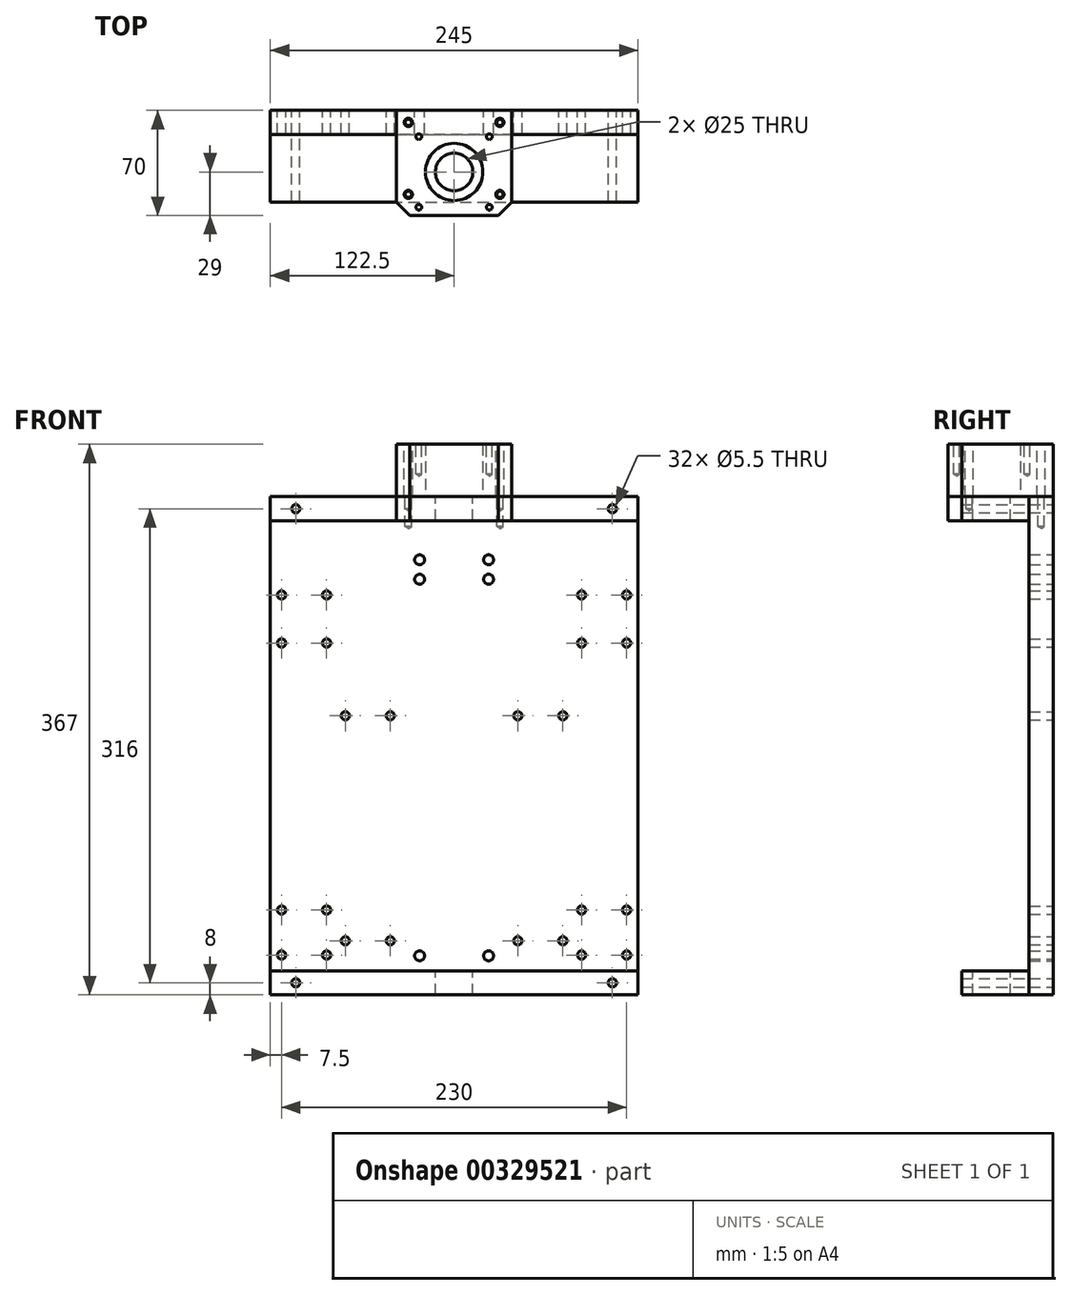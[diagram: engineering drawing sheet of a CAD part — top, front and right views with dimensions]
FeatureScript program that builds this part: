
annotation { "Feature Type Name" : "Feature", "Feature Type Description" : "" }
export const myFeature = defineFeature(function(context is Context, id is Id, definition is map)
    precondition{}
    {
        {
            var Q0;
            Q0=qCreatedBy(makeId("Front.planeOp"),FACE);
            var sketch = newSketch(context, id + "F0", { "sketchPlane" : qUnion([Q0])});
            skLineSegment(sketch, "E0.bottom", {"start": v(120.5, 166) * mm, "end": v(-120.5, 166) * mm});
            skLineSegment(sketch, "E0.top", {"start": v(120.5, -166) * mm, "end": v(-120.5, -166) * mm});
            skLineSegment(sketch, "E0.left", {"start": v(122.5, 164) * mm, "end": v(122.5, -164) * mm});
            skLineSegment(sketch, "E0.right", {"start": v(-122.5, 164) * mm, "end": v(-122.5, -164) * mm});
            skPoint(sketch, "E0.middle", {"position": v(0, 0) * mm});
            skPoint(sketch, "E1.visualSharp", {"position": v(-122.5, 166) * mm});
            skArc(sketch, "E1.filletArc", {"start": v(-120.5, 166) * mm, "mid": v(-121.91, 165.41) * mm, "end": v(-122.5, 164) * mm});
            skPoint(sketch, "E2.visualSharp", {"position": v(122.5, 166) * mm});
            skArc(sketch, "E2.filletArc", {"start": v(122.5, 164) * mm, "mid": v(121.91, 165.41) * mm, "end": v(120.5, 166) * mm});
            skPoint(sketch, "E3.visualSharp", {"position": v(122.5, -166) * mm});
            skArc(sketch, "E3.filletArc", {"start": v(120.5, -166) * mm, "mid": v(121.91, -165.41) * mm, "end": v(122.5, -164) * mm});
            skPoint(sketch, "E4.visualSharp", {"position": v(-122.5, -166) * mm});
            skArc(sketch, "E4.filletArc", {"start": v(-122.5, -164) * mm, "mid": v(-121.91, -165.41) * mm, "end": v(-120.5, -166) * mm});
            skCircle(sketch, "E5", {"center": v(-115, 100.5) * mm, "radius": 2.75 * mm});
            skCircle(sketch, "E6", {"center": v(-85, 100.5) * mm, "radius": 2.75 * mm});
            skCircle(sketch, "E7", {"center": v(-115, 68.5) * mm, "radius": 2.75 * mm});
            skCircle(sketch, "E8", {"center": v(-85, 68.5) * mm, "radius": 2.75 * mm});
            skCircle(sketch, "E9", {"center": v(-115, -109.5) * mm, "radius": 2.75 * mm});
            skCircle(sketch, "E10", {"center": v(-85, -109.5) * mm, "radius": 2.75 * mm});
            skCircle(sketch, "E11", {"center": v(-115, -139.5) * mm, "radius": 2.75 * mm});
            skCircle(sketch, "E12", {"center": v(-85, -139.5) * mm, "radius": 2.75 * mm});
            skCircle(sketch, "E13", {"center": v(85, -109.5) * mm, "radius": 2.75 * mm});
            skCircle(sketch, "E14", {"center": v(115, -109.5) * mm, "radius": 2.75 * mm});
            skCircle(sketch, "E15", {"center": v(85, -139.5) * mm, "radius": 2.75 * mm});
            skCircle(sketch, "E16", {"center": v(115, -139.5) * mm, "radius": 2.75 * mm});
            skCircle(sketch, "E17", {"center": v(85, 100.5) * mm, "radius": 2.75 * mm});
            skCircle(sketch, "E18", {"center": v(115, 100.5) * mm, "radius": 2.75 * mm});
            skCircle(sketch, "E19", {"center": v(85, 68.5) * mm, "radius": 2.75 * mm});
            skCircle(sketch, "E20", {"center": v(115, 68.5) * mm, "radius": 2.75 * mm});
            skCircle(sketch, "E21", {"center": v(-72.5, -130) * mm, "radius": 2.75 * mm});
            skCircle(sketch, "E22", {"center": v(-42.5, -130) * mm, "radius": 2.75 * mm});
            skCircle(sketch, "E23", {"center": v(-72.5, 20) * mm, "radius": 2.75 * mm});
            skCircle(sketch, "E24", {"center": v(-42.5, 20) * mm, "radius": 2.75 * mm});
            skCircle(sketch, "E25", {"center": v(42.5, 20) * mm, "radius": 2.75 * mm});
            skCircle(sketch, "E26", {"center": v(72.5, 20) * mm, "radius": 2.75 * mm});
            skCircle(sketch, "E27", {"center": v(42.5, -130) * mm, "radius": 2.75 * mm});
            skCircle(sketch, "E28", {"center": v(72.5, -130) * mm, "radius": 2.75 * mm});
            skCircle(sketch, "E29", {"center": v(-23, 124) * mm, "radius": 3.3 * mm});
            skCircle(sketch, "E30", {"center": v(23, 124) * mm, "radius": 3.3 * mm});
            skCircle(sketch, "E31", {"center": v(-23, -140) * mm, "radius": 3.3 * mm});
            skCircle(sketch, "E32", {"center": v(23, -140) * mm, "radius": 3.3 * mm});
            skCircle(sketch, "E33", {"center": v(-23, 111) * mm, "radius": 3.3 * mm});
            skCircle(sketch, "E34", {"center": v(23, 111) * mm, "radius": 3.3 * mm});
            skCircle(sketch, "E35", {"center": v(-105.5, 158) * mm, "radius": 2.75 * mm});
            skCircle(sketch, "E36", {"center": v(105.5, 158) * mm, "radius": 2.75 * mm});
            skCircle(sketch, "E37", {"center": v(-105.5, -158) * mm, "radius": 2.75 * mm});
            skCircle(sketch, "E38", {"center": v(105.5, -158) * mm, "radius": 2.75 * mm});
            skSolve(sketch);
        }
        {
            var Q0;
            Q0 = qSketchRegion(id + "F0", true);
            extrude(context, id + "F1", {"entities" : qUnion([Q0]), "depth" : 16 * mm});
        }
        {
            var Q0;
            Q0=makeQuery(id+"F1.opExtrude","CAP_FACE",FACE,{"disambiguationData":[OSD([sQuery(id+"F0.wireOp",EDGE,"E0.bottom"),sQuery(id+"F0.wireOp",EDGE,"E0.top"),sQuery(id+"F0.wireOp",EDGE,"E0.left"),sQuery(id+"F0.wireOp",EDGE,"E0.right"),sQuery(id+"F0.wireOp",EDGE,"E1.filletArc"),sQuery(id+"F0.wireOp",EDGE,"E2.filletArc"),sQuery(id+"F0.wireOp",EDGE,"E3.filletArc"),sQuery(id+"F0.wireOp",EDGE,"E4.filletArc"),sQuery(id+"F0.wireOp",EDGE,"E5"),sQuery(id+"F0.wireOp",EDGE,"E6"),sQuery(id+"F0.wireOp",EDGE,"E7"),sQuery(id+"F0.wireOp",EDGE,"E8"),sQuery(id+"F0.wireOp",EDGE,"E9"),sQuery(id+"F0.wireOp",EDGE,"E10"),sQuery(id+"F0.wireOp",EDGE,"E11"),sQuery(id+"F0.wireOp",EDGE,"E12"),sQuery(id+"F0.wireOp",EDGE,"E13"),sQuery(id+"F0.wireOp",EDGE,"E14"),sQuery(id+"F0.wireOp",EDGE,"E15"),sQuery(id+"F0.wireOp",EDGE,"E16"),sQuery(id+"F0.wireOp",EDGE,"E17"),sQuery(id+"F0.wireOp",EDGE,"E18"),sQuery(id+"F0.wireOp",EDGE,"E19"),sQuery(id+"F0.wireOp",EDGE,"E20"),sQuery(id+"F0.wireOp",EDGE,"E21"),sQuery(id+"F0.wireOp",EDGE,"E22"),sQuery(id+"F0.wireOp",EDGE,"E23"),sQuery(id+"F0.wireOp",EDGE,"E24"),sQuery(id+"F0.wireOp",EDGE,"E25"),sQuery(id+"F0.wireOp",EDGE,"E26"),sQuery(id+"F0.wireOp",EDGE,"E27"),sQuery(id+"F0.wireOp",EDGE,"E28"),sQuery(id+"F0.wireOp",EDGE,"E29"),sQuery(id+"F0.wireOp",EDGE,"E30"),sQuery(id+"F0.wireOp",EDGE,"E31"),sQuery(id+"F0.wireOp",EDGE,"E32"),sQuery(id+"F0.wireOp",EDGE,"E33"),sQuery(id+"F0.wireOp",EDGE,"E34"),sQuery(id+"F0.wireOp",EDGE,"E35"),sQuery(id+"F0.wireOp",EDGE,"E36"),sQuery(id+"F0.wireOp",EDGE,"E37"),sQuery(id+"F0.wireOp",EDGE,"E38")])],"isStart":false});
            var sketch = newSketch(context, id + "F2", { "sketchPlane" : qUnion([Q0])});
            skLineSegment(sketch, "E39.bottom", {"start": v(-122.5, 166) * mm, "end": v(122.5, 166) * mm});
            skLineSegment(sketch, "E39.top", {"start": v(-122.5, 150) * mm, "end": v(122.5, 150) * mm});
            skLineSegment(sketch, "E39.left", {"start": v(-122.5, 166) * mm, "end": v(-122.5, 150) * mm});
            skLineSegment(sketch, "E39.right", {"start": v(122.5, 166) * mm, "end": v(122.5, 150) * mm});
            skCircle(sketch, "E40", {"center": v(-105.5, 158) * mm, "radius": 2.75 * mm});
            skCircle(sketch, "E41", {"center": v(105.5, 158) * mm, "radius": 2.75 * mm});
            skLineSegment(sketch, "E42.bottom", {"start": v(-122.5, -150) * mm, "end": v(122.5, -150) * mm});
            skLineSegment(sketch, "E42.top", {"start": v(-122.5, -166) * mm, "end": v(122.5, -166) * mm});
            skLineSegment(sketch, "E42.left", {"start": v(-122.5, -150) * mm, "end": v(-122.5, -166) * mm});
            skLineSegment(sketch, "E42.right", {"start": v(122.5, -150) * mm, "end": v(122.5, -166) * mm});
            skCircle(sketch, "E43", {"center": v(-105.5, -158) * mm, "radius": 2.75 * mm});
            skCircle(sketch, "E44", {"center": v(105.5, -158) * mm, "radius": 2.75 * mm});
            skSolve(sketch);
        }
        {
            var Q0;
            Q0 = qSketchRegion(id + "F2", true);
            extrude(context, id + "F3", {"entities" : qUnion([Q0]), "depth" : 45 * mm});
        }
        {
            var Q0;
            Q0=makeQuery(id+"F3.opExtrude","SWEPT_FACE",FACE,{"disambiguationData":[OSD([sQuery(id+"F2.wireOp",EDGE,"E39.bottom")])]});
            var sketch = newSketch(context, id + "F4", { "sketchPlane" : qUnion([Q0])});
            skCircle(sketch, "E45", {"center": v(0, -41) * mm, "radius": 12.5 * mm});
            skSolve(sketch);
        }
        {
            var Q0;
            Q0 = qSketchRegion(id + "F4", true);
            extrude(context, id + "F5", {"entities" : qUnion([Q0]), "operationType" : NewBodyOperationType.REMOVE, "endBound" : BoundingType.THROUGH_ALL, "oppositeDirection" : true, "depth" : 25 * mm});
        }
        {
            var Q0;
            Q0=makeQuery(id+"F3.opExtrude","SWEPT_FACE",FACE,{"disambiguationData":[OSD([sQuery(id+"F2.wireOp",EDGE,"E39.bottom")])]});
            var sketch = newSketch(context, id + "F6", { "sketchPlane" : qUnion([Q0])});
            skLineSegment(sketch, "E46", {"start": v(-38.5, -61) * mm, "end": v(-29.5, -70) * mm});
            skLineSegment(sketch, "E47", {"start": v(-29.5, -70) * mm, "end": v(29.5, -70) * mm});
            skLineSegment(sketch, "E48", {"start": v(29.5, -70) * mm, "end": v(38.5, -61) * mm});
            skLineSegment(sketch, "E49", {"start": v(38.5, -61) * mm, "end": v(-38.5, -61) * mm});
            skPoint(sketch, "E50", {"position": v(0, -41) * mm});
            skSolve(sketch);
        }
        {
            var Q0;
            Q0 = qSketchRegion(id + "F6", true);
            extrude(context, id + "F7", {"entities" : qUnion([Q0]), "operationType" : NewBodyOperationType.ADD, "oppositeDirection" : true, "depth" : 16 * mm});
        }
        {
            var Q0;
            Q0=makeQuery(id+"F7.boolean.opBoolean","MERGE",FACE,{"derivedFrom":[makeQuery(id+"F3.opExtrude","SWEPT_FACE",FACE,{"disambiguationData":[OSD([sQuery(id+"F2.wireOp",EDGE,"E39.bottom")])]}),makeQuery(id+"F7.opExtrude","CAP_FACE",FACE,{"disambiguationData":[OSD([sQuery(id+"F6.wireOp",EDGE,"E46"),sQuery(id+"F6.wireOp",EDGE,"E47"),sQuery(id+"F6.wireOp",EDGE,"E48"),sQuery(id+"F6.wireOp",EDGE,"E49")])],"isStart":true})]});
            var sketch = newSketch(context, id + "F8", { "sketchPlane" : qUnion([Q0])});
            skLineSegment(sketch, "E51", {"start": v(-29.5, -70) * mm, "end": v(-38.5, -61) * mm});
            skLineSegment(sketch, "E52", {"start": v(-38.5, -61) * mm, "end": v(-38.5, 0) * mm});
            skLineSegment(sketch, "E53", {"start": v(-38.5, 0) * mm, "end": v(38.5, 0) * mm});
            skLineSegment(sketch, "E54", {"start": v(38.5, 0) * mm, "end": v(38.5, -61) * mm});
            skLineSegment(sketch, "E55", {"start": v(38.5, -61) * mm, "end": v(29.5, -70) * mm});
            skLineSegment(sketch, "E56", {"start": v(29.5, -70) * mm, "end": v(-29.5, -70) * mm});
            skCircle(sketch, "E57", {"center": v(0, -41) * mm, "radius": 19.1 * mm});
            skSolve(sketch);
        }
        {
            var Q0;
            Q0 = qSketchRegion(id + "F8", true);
            extrude(context, id + "F9", {"entities" : qUnion([Q0]), "depth" : 35 * mm});
        }
        {
            var Q0;
            Q0=makeQuery(id+"F9.opExtrude","CAP_FACE",FACE,{"disambiguationData":[OSD([sQuery(id+"F8.wireOp",EDGE,"E51"),sQuery(id+"F8.wireOp",EDGE,"E52"),sQuery(id+"F8.wireOp",EDGE,"E53"),sQuery(id+"F8.wireOp",EDGE,"E54"),sQuery(id+"F8.wireOp",EDGE,"E55"),sQuery(id+"F8.wireOp",EDGE,"E56"),sQuery(id+"F8.wireOp",EDGE,"E57")])],"isStart":false});
            var sketch = newSketch(context, id + "F10", { "sketchPlane" : qUnion([Q0])});
            skPoint(sketch, "E58", {"position": v(-30.5, -8) * mm});
            skPoint(sketch, "E59", {"position": v(30.5, -8) * mm});
            skPoint(sketch, "E60", {"position": v(-23.5, -64.5) * mm});
            skPoint(sketch, "E61", {"position": v(-23.5, -17.5) * mm});
            skPoint(sketch, "E62", {"position": v(23.5, -17.5) * mm});
            skPoint(sketch, "E63", {"position": v(23.5, -64.5) * mm});
            skPoint(sketch, "E64", {"position": v(0, -41) * mm});
            skPoint(sketch, "E65", {"position": v(-30.5, -56) * mm});
            skPoint(sketch, "E66", {"position": v(30.5, -56) * mm});
            skSolve(sketch);
        }
        {
            var Q0;
            Q0=sQuery(id+"F10.wireOp",VERTEX,"E61");
            var Q1;
            Q1=sQuery(id+"F10.wireOp",VERTEX,"E60");
            var Q2;
            Q2=sQuery(id+"F10.wireOp",VERTEX,"E63");
            var Q3;
            Q3=sQuery(id+"F10.wireOp",VERTEX,"E62");
            var Q4;
            Q4=makeQuery(id+"F9.opExtrude","SWEPT_BODY",BODY,{"disambiguationData":[OSD([sQuery(id+"F8.wireOp",EDGE,"E51"),sQuery(id+"F8.wireOp",EDGE,"E52"),sQuery(id+"F8.wireOp",EDGE,"E53"),sQuery(id+"F8.wireOp",EDGE,"E54"),sQuery(id+"F8.wireOp",EDGE,"E55"),sQuery(id+"F8.wireOp",EDGE,"E56"),sQuery(id+"F8.wireOp",EDGE,"E57")])]});
            hole(context, id + "F11", {"style" : HoleStyle.SIMPLE, "endStyle" : HoleEndStyle.BLIND, "standardTappedOrClearance" : lookupTablePath({ "standard" : "ANSI", "engagement" : "75%", "pitch" : "24 tpi", "size" : "#10", "type" : "Tapped" }), "standardBlindInLast" : lookupTablePath({ "standard" : "ANSI", "engagement" : "75%", "pitch" : "24 tpi", "size" : "#10", "type" : "Tapped" }), "holeDiameter" : 3.8 * mm, "showTappedDepth" : true, "holeDepth" : 20 * mm, "tappedDepth" : 16.82 * mm, "tapClearance" : 3, "locations" : qUnion([Q0, Q1, Q2, Q3]), "scope" : qUnion([Q4]), "majorDiameter" : 4.83 * mm});
        }
        {
            var Q0;
            Q0=sQuery(id+"F10.wireOp",VERTEX,"E58");
            var Q1;
            Q1=sQuery(id+"F10.wireOp",VERTEX,"E59");
            var Q2;
            Q2=makeQuery(id+"F9.opExtrude","SWEPT_BODY",BODY,{"disambiguationData":[OSD([sQuery(id+"F8.wireOp",EDGE,"E51"),sQuery(id+"F8.wireOp",EDGE,"E52"),sQuery(id+"F8.wireOp",EDGE,"E53"),sQuery(id+"F8.wireOp",EDGE,"E54"),sQuery(id+"F8.wireOp",EDGE,"E55"),sQuery(id+"F8.wireOp",EDGE,"E56"),sQuery(id+"F8.wireOp",EDGE,"E57")])]});
            var Q3;
            Q3=makeQuery(id+"F1.opExtrude","SWEPT_BODY",BODY,{"disambiguationData":[OSD([sQuery(id+"F0.wireOp",EDGE,"E0.bottom"),sQuery(id+"F0.wireOp",EDGE,"E0.top"),sQuery(id+"F0.wireOp",EDGE,"E0.left"),sQuery(id+"F0.wireOp",EDGE,"E0.right"),sQuery(id+"F0.wireOp",EDGE,"E1.filletArc"),sQuery(id+"F0.wireOp",EDGE,"E2.filletArc"),sQuery(id+"F0.wireOp",EDGE,"E3.filletArc"),sQuery(id+"F0.wireOp",EDGE,"E4.filletArc"),sQuery(id+"F0.wireOp",EDGE,"E5"),sQuery(id+"F0.wireOp",EDGE,"E6"),sQuery(id+"F0.wireOp",EDGE,"E7"),sQuery(id+"F0.wireOp",EDGE,"E8"),sQuery(id+"F0.wireOp",EDGE,"E9"),sQuery(id+"F0.wireOp",EDGE,"E10"),sQuery(id+"F0.wireOp",EDGE,"E11"),sQuery(id+"F0.wireOp",EDGE,"E12"),sQuery(id+"F0.wireOp",EDGE,"E13"),sQuery(id+"F0.wireOp",EDGE,"E14"),sQuery(id+"F0.wireOp",EDGE,"E15"),sQuery(id+"F0.wireOp",EDGE,"E16"),sQuery(id+"F0.wireOp",EDGE,"E17"),sQuery(id+"F0.wireOp",EDGE,"E18"),sQuery(id+"F0.wireOp",EDGE,"E19"),sQuery(id+"F0.wireOp",EDGE,"E20"),sQuery(id+"F0.wireOp",EDGE,"E21"),sQuery(id+"F0.wireOp",EDGE,"E22"),sQuery(id+"F0.wireOp",EDGE,"E23"),sQuery(id+"F0.wireOp",EDGE,"E24"),sQuery(id+"F0.wireOp",EDGE,"E25"),sQuery(id+"F0.wireOp",EDGE,"E26"),sQuery(id+"F0.wireOp",EDGE,"E27"),sQuery(id+"F0.wireOp",EDGE,"E28"),sQuery(id+"F0.wireOp",EDGE,"E29"),sQuery(id+"F0.wireOp",EDGE,"E30"),sQuery(id+"F0.wireOp",EDGE,"E31"),sQuery(id+"F0.wireOp",EDGE,"E32"),sQuery(id+"F0.wireOp",EDGE,"E33"),sQuery(id+"F0.wireOp",EDGE,"E34"),sQuery(id+"F0.wireOp",EDGE,"E35"),sQuery(id+"F0.wireOp",EDGE,"E36"),sQuery(id+"F0.wireOp",EDGE,"E37"),sQuery(id+"F0.wireOp",EDGE,"E38")])]});
            hole(context, id + "F12", {"style" : HoleStyle.C_BORE, "endStyle" : HoleEndStyle.BLIND, "holeDiameter" : 4.2 * mm, "cBoreDiameter" : 5.5 * mm, "cBoreDepth" : 35 * mm, "holeDepth" : 55 * mm, "tappedDepth" : 16.82 * mm, "tapClearance" : 3, "locations" : qUnion([Q0, Q1]), "scope" : qUnion([Q2, Q3])});
        }
        {
            var Q0;
            Q0=sQuery(id+"F10.wireOp",VERTEX,"E65");
            var Q1;
            Q1=sQuery(id+"F10.wireOp",VERTEX,"E66");
            var Q2;
            Q2=makeQuery(id+"F3.opExtrude","SWEPT_BODY",BODY,{"disambiguationData":[OSD([sQuery(id+"F2.wireOp",EDGE,"E39.bottom"),sQuery(id+"F2.wireOp",EDGE,"E39.top"),sQuery(id+"F2.wireOp",EDGE,"E39.left"),sQuery(id+"F2.wireOp",EDGE,"E39.right"),sQuery(id+"F2.wireOp",EDGE,"E40"),sQuery(id+"F2.wireOp",EDGE,"E41")])]});
            var Q3;
            Q3=makeQuery(id+"F9.opExtrude","SWEPT_BODY",BODY,{"disambiguationData":[OSD([sQuery(id+"F8.wireOp",EDGE,"E51"),sQuery(id+"F8.wireOp",EDGE,"E52"),sQuery(id+"F8.wireOp",EDGE,"E53"),sQuery(id+"F8.wireOp",EDGE,"E54"),sQuery(id+"F8.wireOp",EDGE,"E55"),sQuery(id+"F8.wireOp",EDGE,"E56"),sQuery(id+"F8.wireOp",EDGE,"E57")])]});
            hole(context, id + "F13", {"style" : HoleStyle.C_BORE, "endStyle" : HoleEndStyle.BLIND, "holeDiameter" : 4.2 * mm, "cBoreDiameter" : 5.5 * mm, "cBoreDepth" : 35 * mm, "holeDepth" : 43 * mm, "tappedDepth" : 16.82 * mm, "tapClearance" : 3, "locations" : qUnion([Q0, Q1]), "scope" : qUnion([Q2, Q3])});
        }
    });
